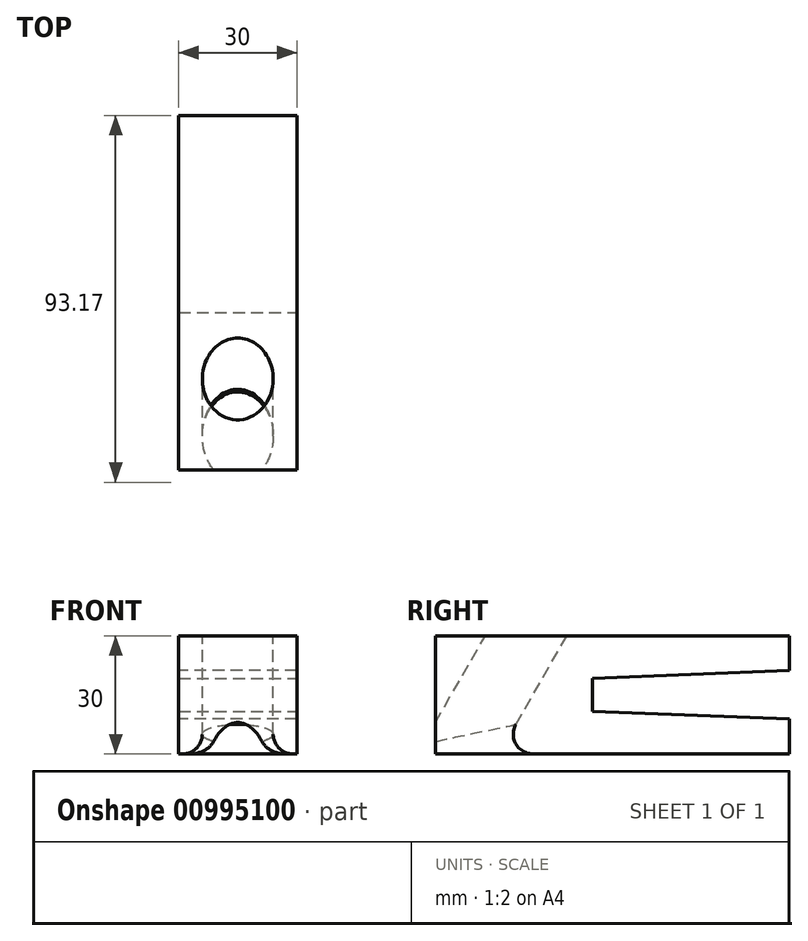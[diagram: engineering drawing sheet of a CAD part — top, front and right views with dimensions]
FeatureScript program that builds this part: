
annotation { "Feature Type Name" : "Feature", "Feature Type Description" : "" }
export const myFeature = defineFeature(function(context is Context, id is Id, definition is map)
    precondition{}
    {
        {
            var Q0;
            Q0=qCreatedBy(makeId("Front.planeOp"),FACE);
            var sketch = newSketch(context, id + "F0", { "sketchPlane" : qUnion([Q0])});
            skLineSegment(sketch, "E0.bottom", {"start": v(0, 0) * mm, "end": v(30, 0) * mm});
            skLineSegment(sketch, "E0.top", {"start": v(0, 30) * mm, "end": v(30, 30) * mm});
            skLineSegment(sketch, "E0.left", {"start": v(0, 0) * mm, "end": v(0, 30) * mm});
            skLineSegment(sketch, "E0.right", {"start": v(30, 0) * mm, "end": v(30, 30) * mm});
            skSolve(sketch);
        }
        {
            var Q0;
            Q0=qSketchRegion(id+"F0",true);
            extrude(context, id + "F1", {"entities" : qUnion([Q0]), "depth" : 40 * mm, "offsetDistance" : 25 * mm});
        }
        {
            var Q0;
            Q0=makeQuery(id+"F1.opExtrude","CAP_FACE",FACE,{"disambiguationData":[OSD([sQuery(id+"F0.wireOp",EDGE,"E0.bottom"),sQuery(id+"F0.wireOp",EDGE,"E0.top"),sQuery(id+"F0.wireOp",EDGE,"E0.left"),sQuery(id+"F0.wireOp",EDGE,"E0.right")])],"isStart":true});
            var sketch = newSketch(context, id + "F2", { "sketchPlane" : qUnion([Q0])});
            skLineSegment(sketch, "E1.bottom", {"start": v(0, 0) * mm, "end": v(-30, 0) * mm});
            skLineSegment(sketch, "E1.top", {"start": v(0, 10.85) * mm, "end": v(-30, 10.85) * mm});
            skLineSegment(sketch, "E1.left", {"start": v(0, 0) * mm, "end": v(0, 10.85) * mm});
            skLineSegment(sketch, "E1.right", {"start": v(-30, 0) * mm, "end": v(-30, 10.85) * mm});
            skLineSegment(sketch, "E2.bottom", {"start": v(0, 30) * mm, "end": v(-30, 30) * mm});
            skLineSegment(sketch, "E2.top", {"start": v(0, 19.15) * mm, "end": v(-30, 19.15) * mm});
            skLineSegment(sketch, "E2.left", {"start": v(0, 30) * mm, "end": v(0, 19.15) * mm});
            skLineSegment(sketch, "E2.right", {"start": v(-30, 30) * mm, "end": v(-30, 19.15) * mm});
            skLineSegment(sketch, "E3", {"start": v(0, 10.85) * mm, "end": v(0, 19.15) * mm});
            skSolve(sketch);
        }
        {
            var Q0;
            Q0=qSketchRegion(id+"F2",true);
            extrude(context, id + "F3", {"entities" : qUnion([Q0]), "operationType" : NewBodyOperationType.ADD, "depth" : 50 * mm, "offsetDistance" : 25 * mm});
        }
        {
            var Q0;
            Q0=makeQuery(id+"F3.boolean.opBoolean","MERGE",FACE,{"derivedFrom":[makeQuery(id+"F1.opExtrude","SWEPT_FACE",FACE,{"disambiguationData":[OSD([sQuery(id+"F0.wireOp",EDGE,"E0.left")])]}),makeQuery(id+"F3.opExtrude","SWEPT_FACE",FACE,{"disambiguationData":[OSD([sQuery(id+"F2.wireOp",EDGE,"E1.left")])]}),makeQuery(id+"F3.opExtrude","SWEPT_FACE",FACE,{"disambiguationData":[OSD([sQuery(id+"F2.wireOp",EDGE,"E2.left")])]})]});
            var sketch = newSketch(context, id + "F4", { "sketchPlane" : qUnion([Q0])});
            skLineSegment(sketch, "E4", {"start": v(0, 19.15) * mm, "end": v(-50, 21.15) * mm});
            skLineSegment(sketch, "E5", {"start": v(-50, 21.15) * mm, "end": v(-50, 19.15) * mm});
            skLineSegment(sketch, "E6", {"start": v(-50, 19.15) * mm, "end": v(0, 19.15) * mm});
            skLineSegment(sketch, "E7", {"start": v(0, 10.85) * mm, "end": v(-50, 8.85) * mm});
            skLineSegment(sketch, "E8", {"start": v(-50, 8.85) * mm, "end": v(-50, 10.85) * mm});
            skLineSegment(sketch, "E9", {"start": v(-50, 10.85) * mm, "end": v(0, 10.85) * mm});
            skSolve(sketch);
        }
        {
            var Q0;
            Q0=qSketchRegion(id+"F4",true);
            extrude(context, id + "F5", {"entities" : qUnion([Q0]), "operationType" : NewBodyOperationType.REMOVE, "endBound" : BoundingType.UP_TO_NEXT, "oppositeDirection" : true, "depth" : 25 * mm, "offsetDistance" : 25 * mm});
        }
        {
            var Q0;
            Q0=makeQuery(id+"F1.opExtrude","CAP_EDGE",EDGE,{"disambiguationData":[OSD([sQuery(id+"F0.wireOp",EDGE,"E0.bottom")])],"isStart":false});
            cPlane(context, id + "F6", {"entities" : qUnion([Q0]), "cplaneType" : CPlaneType.LINE_ANGLE, "offset" : 25 * mm, "angle" : 60 * degree, "width" : 150 * mm, "height" : 150 * mm});
        }
        {
            var Q0;
            Q0=qCreatedBy(id+"F6.planeOp",FACE);
            cPlane(context, id + "F7", {"entities" : qUnion([Q0]), "cplaneType" : CPlaneType.OFFSET, "offset" : 30.9 * mm, "width" : 150 * mm, "height" : 150 * mm});
        }
        {
            var Q0;
            Q0=qCreatedBy(id+"F7.planeOp",FACE);
            var sketch = newSketch(context, id + "F8", { "sketchPlane" : qUnion([Q0])});
            skCircle(sketch, "E10", {"center": v(15, -29.64) * mm, "radius": 9 * mm});
            skSolve(sketch);
        }
        {
            var Q0;
            Q0=qSketchRegion(id+"F8",true);
            extrude(context, id + "F9", {"entities" : qUnion([Q0]), "operationType" : NewBodyOperationType.REMOVE, "endBound" : BoundingType.THROUGH_ALL, "oppositeDirection" : true, "depth" : 25 * mm, "offsetDistance" : 25 * mm, "hasSecondDirection" : true, "secondDirectionOppositeDirection" : false, "secondDirectionDepth" : 25 * mm});
        }
        {
            var Q0;
            Q0=makeQuery(id+"F9.boolean.opBoolean","INTERSECT",EDGE,{"derivedFrom":[makeQuery(id+"F3.boolean.opBoolean","MERGE",FACE,{"derivedFrom":[makeQuery(id+"F1.opExtrude","SWEPT_FACE",FACE,{"disambiguationData":[OSD([sQuery(id+"F0.wireOp",EDGE,"E0.bottom")])]}),makeQuery(id+"F3.opExtrude","SWEPT_FACE",FACE,{"disambiguationData":[OSD([sQuery(id+"F2.wireOp",EDGE,"E1.bottom")])]})]}),makeQuery(id+"F9.opExtrude","SWEPT_FACE",FACE,{"disambiguationData":[OSD([sQuery(id+"F8.wireOp",EDGE,"E10")])]})]});
            fillet(context, id + "F10", {"entities" : qUnion([Q0]), "radius" : 5 * mm, "tangentPropagation" : true, "allowEdgeOverflow" : false});
        }
    });
